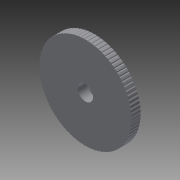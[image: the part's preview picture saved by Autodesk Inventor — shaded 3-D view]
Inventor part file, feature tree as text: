
AUTODESK INVENTOR PART (.ipt)
format: ipt  version: 2014 (Build 180170000, 170)  size: 279,040 bytes
history: native  units: mm
features: extrude x3, sketch x3, pattern_circular x1
ambient origin geometry x8: Origin, YZ Plane, XZ Plane, XY Plane, X Axis, Y Axis, Z Axis, Center Point
bodies: Solid1 (feature_tree)
feature tree (7):
  extrude  "Extrusion1"  Depth=6.0mm TaperAngle=0.0deg
  extrude  "Extrusion2"  Depth=10.0mm TaperAngle=0.0deg
  extrude  "Extrusion3"  Depth=10.0mm TaperAngle=360.0deg
  pattern_circular  "Circular Pattern1"  [2 undecoded]
  sketch  "Sketch1"  dims[d0=60.0mm d1=6.0mm d2=0.0mm]
  sketch  "Sketch2"  dims[d3=10.0mm d4=10.0mm d5=0.0mm]
  sketch  "Sketch3"  dims[d7=10.0mm d8=0.0mm d9=800.0mm d10=360.0deg]
note: 2 required parameter values undecoded (feature->parameter linkage not recoverable at this tier; creation-order binding heuristic only, values carry confidence <= 0.55)
